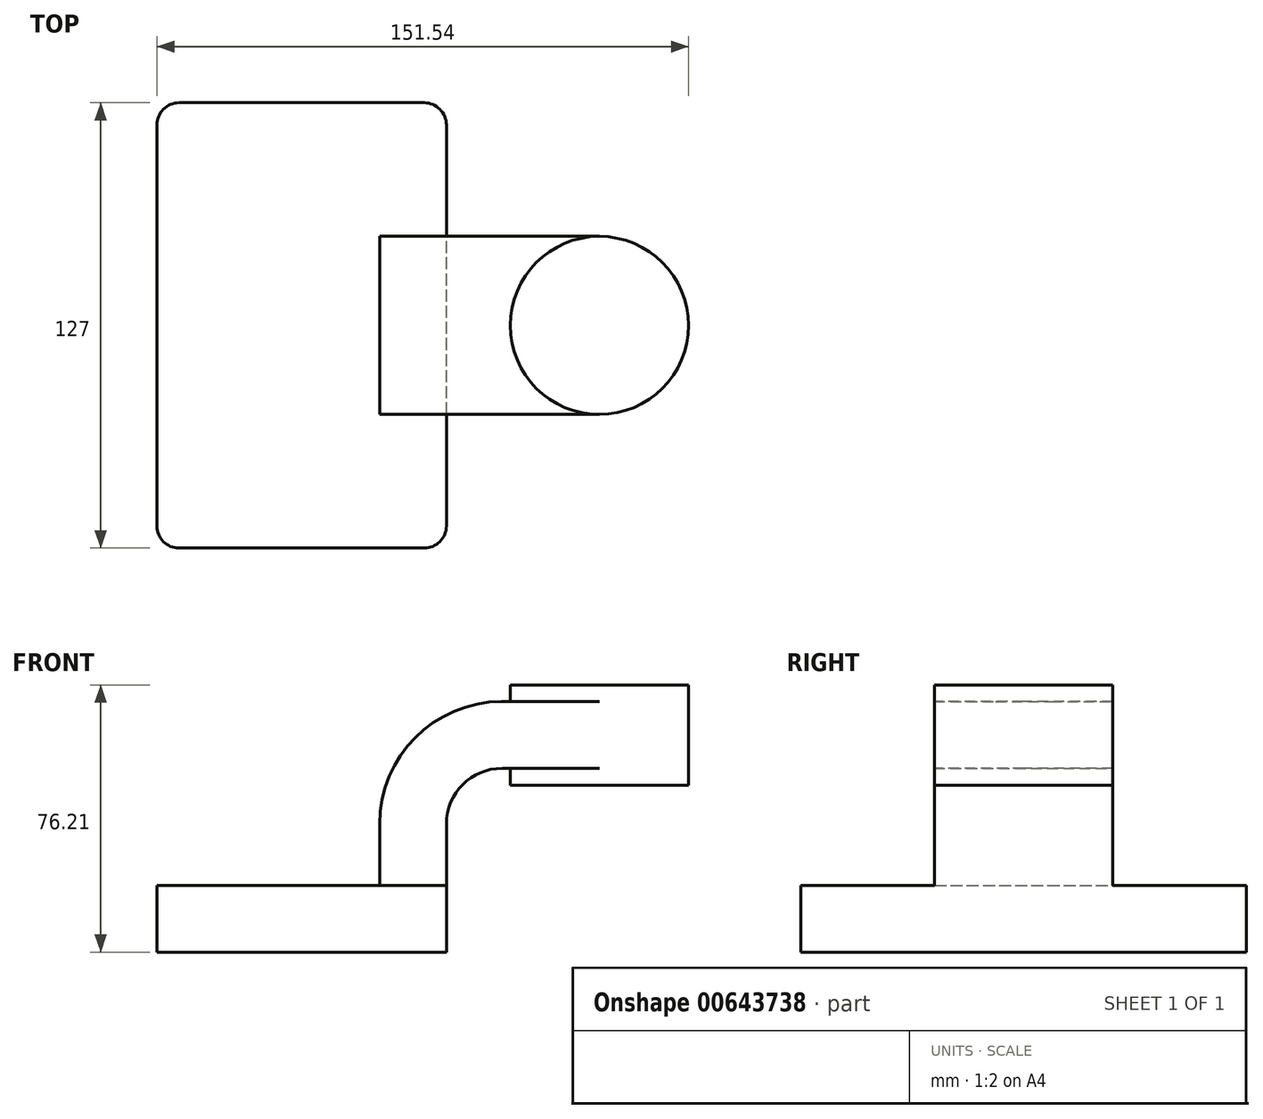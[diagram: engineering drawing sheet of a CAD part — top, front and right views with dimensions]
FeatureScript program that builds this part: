
annotation { "Feature Type Name" : "Feature", "Feature Type Description" : "" }
export const myFeature = defineFeature(function(context is Context, id is Id, definition is map)
    precondition{}
    {
        {
            var Q0;
            Q0=qCreatedBy(makeId("Front.planeOp"),FACE);
            var sketch = newSketch(context, id + "F0", { "sketchPlane" : qUnion([Q0])});
            skLineSegment(sketch, "E0.bottom", {"start": v(-41.28, -9.52) * mm, "end": v(41.28, -9.52) * mm});
            skLineSegment(sketch, "E0.top", {"start": v(-41.28, 9.53) * mm, "end": v(41.28, 9.53) * mm});
            skLineSegment(sketch, "E0.left", {"start": v(-41.28, -9.52) * mm, "end": v(-41.28, 9.53) * mm});
            skLineSegment(sketch, "E0.right", {"start": v(41.28, -9.53) * mm, "end": v(41.28, 9.52) * mm});
            skPoint(sketch, "E0.middle", {"position": v(0, 0) * mm});
            skLineSegment(sketch, "E1.bottom", {"start": v(110.27, 38.1) * mm, "end": v(59.47, 38.1) * mm});
            skLineSegment(sketch, "E1.top", {"start": v(110.27, 66.67) * mm, "end": v(59.47, 66.67) * mm});
            skLineSegment(sketch, "E1.left", {"start": v(110.27, 38.1) * mm, "end": v(110.27, 66.67) * mm});
            skLineSegment(sketch, "E1.right", {"start": v(59.47, 38.1) * mm, "end": v(59.47, 66.67) * mm});
            skPoint(sketch, "E1.middle", {"position": v(84.87, 52.39) * mm});
            skLineSegment(sketch, "E2", {"start": v(41.27, 9.52) * mm, "end": v(41.27, 27) * mm});
            skArc(sketch, "E3", {"start": v(41.27, 27) * mm, "mid": v(45.92, 38.23) * mm, "end": v(57.15, 42.88) * mm});
            skLineSegment(sketch, "E4", {"start": v(57.15, 42.88) * mm, "end": v(84.87, 42.88) * mm});
            skLineSegment(sketch, "E5.0", {"start": v(57.15, 61.93) * mm, "end": v(84.87, 61.93) * mm});
            skArc(sketch, "E5.1", {"start": v(22.23, 27) * mm, "mid": v(32.45, 51.7) * mm, "end": v(57.15, 61.93) * mm});
            skLineSegment(sketch, "E5.2", {"start": v(22.22, 9.52) * mm, "end": v(22.22, 27) * mm});
            skFitSpline(sketch, "E6", {"points": [v(-41.28, 9.52) * mm, v(57.15, 61.93) * mm], "startDerivative": vector(0.39, 109.64) * mm, "endDerivative": vector(209.88, 0.41) * mm});
            skLineSegment(sketch, "E7", {"start": v(84.87, 38.1) * mm, "end": v(84.87, 66.67) * mm});
            skSolve(sketch);
        }
        {
            var Q0;
            Q0=makeQuery(id+"F0.imprint","IMPRINT",FACE,{"disambiguationData":[TD([[makeQuery(id+"F0.imprint","IMPRINT",EDGE,{"derivedFrom":sQuery(id+"F0.wireOp",EDGE,"E0.bottom")}),1.0]])]});
            extrude(context, id + "F1", {"entities" : qUnion([Q0]), "endBound" : BoundingType.SYMMETRIC, "depth" : 127 * mm, "offsetDistance" : 25.4 * mm});
        }
        {
            var Q0;
            {var subQ1=sQuery(id+"F0.wireOp",EDGE,"E2");Q0=makeQuery(id+"F0.imprint","IMPRINT",FACE,{"disambiguationData":[TD([[makeQuery(id+"F0.imprint","IMPRINT",EDGE,{"derivedFrom":subQ1}),1.0]])]});}
            var Q1;
            {var subQ0=sQuery(id+"F0.wireOp",EDGE,"E4");var subQ1=sQuery(id+"F0.wireOp",EDGE,"E1.right");var subQ2=makeQuery(id+"F0.imprint","INTERSECT",VERTEX,{"derivedFrom":[subQ1,subQ0]});Q1=makeQuery(id+"F0.imprint","IMPRINT",FACE,{"disambiguationData":[TD([[makeQuery(id+"F0.imprint","IMPRINT",EDGE,{"disambiguationData":[TD([[subQ2,-1.0]])],"derivedFrom":subQ1}),-1.0]])]});}
            extrude(context, id + "F2", {"entities" : qUnion([Q0, Q1]), "operationType" : NewBodyOperationType.ADD, "endBound" : BoundingType.SYMMETRIC, "depth" : 50.8 * mm, "offsetDistance" : 25.4 * mm});
        }
        {
            var Q0;
            {var subQ4=sQuery(id+"F0.wireOp",EDGE,"E5.1");Q0=makeQuery(id+"F0.imprint","IMPRINT",FACE,{"disambiguationData":[TD([[makeQuery(id+"F0.imprint","IMPRINT",EDGE,{"derivedFrom":subQ4}),1.0]])]});}
            extrude(context, id + "F3", {"entities" : qUnion([Q0]), "operationType" : NewBodyOperationType.ADD, "endBound" : BoundingType.SYMMETRIC, "depth" : 15.88 * mm, "offsetDistance" : 25.4 * mm});
        }
        {
            var Q0;
            {var subQ4=sQuery(id+"F0.wireOp",EDGE,"E1.left");Q0=makeQuery(id+"F0.imprint","IMPRINT",FACE,{"disambiguationData":[TD([[makeQuery(id+"F0.imprint","IMPRINT",EDGE,{"derivedFrom":subQ4}),1.0]])]});}
            var Q1;
            Q1=sQuery(id+"F0.wireOp",EDGE,"E7");
            revolve(context, id + "F4", {"operationType" : NewBodyOperationType.ADD, "entities" : qUnion([Q0]), "axis" : qUnion([Q1]), "revolveType" : RevolveType.FULL});
        }
        {
            var Q0;
            Q0=makeQuery(id+"F1.opExtrude","CAP_EDGE",EDGE,{"disambiguationData":[OSD([sQuery(id+"F0.wireOp",EDGE,"E0.left")])],"isStart":false});
            var Q1;
            Q1=makeQuery(id+"F1.opExtrude","CAP_EDGE",EDGE,{"disambiguationData":[OSD([sQuery(id+"F0.wireOp",EDGE,"E0.right")])],"isStart":false});
            var Q2;
            Q2=makeQuery(id+"F1.opExtrude","CAP_EDGE",EDGE,{"disambiguationData":[OSD([sQuery(id+"F0.wireOp",EDGE,"E0.right")])],"isStart":true});
            var Q3;
            Q3=makeQuery(id+"F1.opExtrude","CAP_EDGE",EDGE,{"disambiguationData":[OSD([sQuery(id+"F0.wireOp",EDGE,"E0.left")])],"isStart":true});
            fillet(context, id + "F5", {"entities" : qUnion([Q0, Q1, Q2, Q3]), "radius" : 6.35 * mm, "tangentPropagation" : true, "allowEdgeOverflow" : false});
        }
    });
